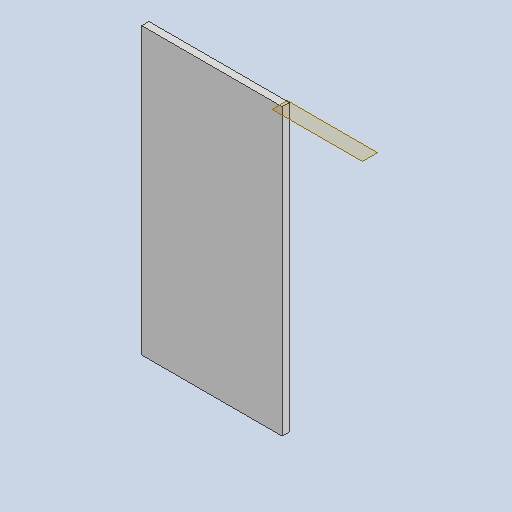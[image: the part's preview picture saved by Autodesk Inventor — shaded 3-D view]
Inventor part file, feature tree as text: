
AUTODESK INVENTOR PART (.ipt)
format: ipt  version: 2023 (Build 270158000, 158)  size: 142,848 bytes
history: native  units: mm
features: other x3, plane x2, sketch x1, extrude x1, reference x1
ambient origin geometry x8: Origin, YZ Plane, XZ Plane, XY Plane, X Axis, Y Axis, Z Axis, Center Point
bodies: Solid1 (feature_tree)
feature tree (8):
  plane  "Work Plane1"
  sketch  "Sketch1"  dims[d0=3.0mm d1=300.0mm d2=10.0mm d3=0.0mm]
  plane  "Work Plane2"
  extrude  "Extrusion1"  Depth=300.0mm
  reference  "Reference1"
  parser-record x1  (decoder bookkeeping rows leaked as tree rows — omitted from the tree; the rows remain in map.json)
  other  "Assembly_V7.iam"
  other  "moulding:1"
note: 1 file-system path scrubbed to <path> (originals preserved in map.json)
